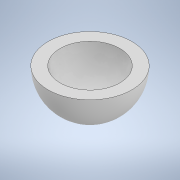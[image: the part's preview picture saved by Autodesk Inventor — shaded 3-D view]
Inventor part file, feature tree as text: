
AUTODESK INVENTOR PART (.ipt)
format: ipt  version: 2022 (Build 260153000, 153)  size: 148,992 bytes
history: native  units: in
note: dims shown in document units (in); Inventor stores cm internally (conversion verified against a paired STEP export)
features: revolve x1, shell x1, sketch x1
ambient origin geometry x8: Origin, YZ Plane, XZ Plane, XY Plane, X Axis, Y Axis, Z Axis, Center Point
bodies: Solid1 (feature_tree)
feature tree (3):
  revolve  "Revolution1"  [1 undecoded]
  shell  "Shell1"  [1 undecoded]
  sketch  "Sketch1"  dims[d3=90.0deg d4=0.3in]
note: 2 required parameter values undecoded (feature->parameter linkage not recoverable at this tier; creation-order binding heuristic only, values carry confidence <= 0.55)